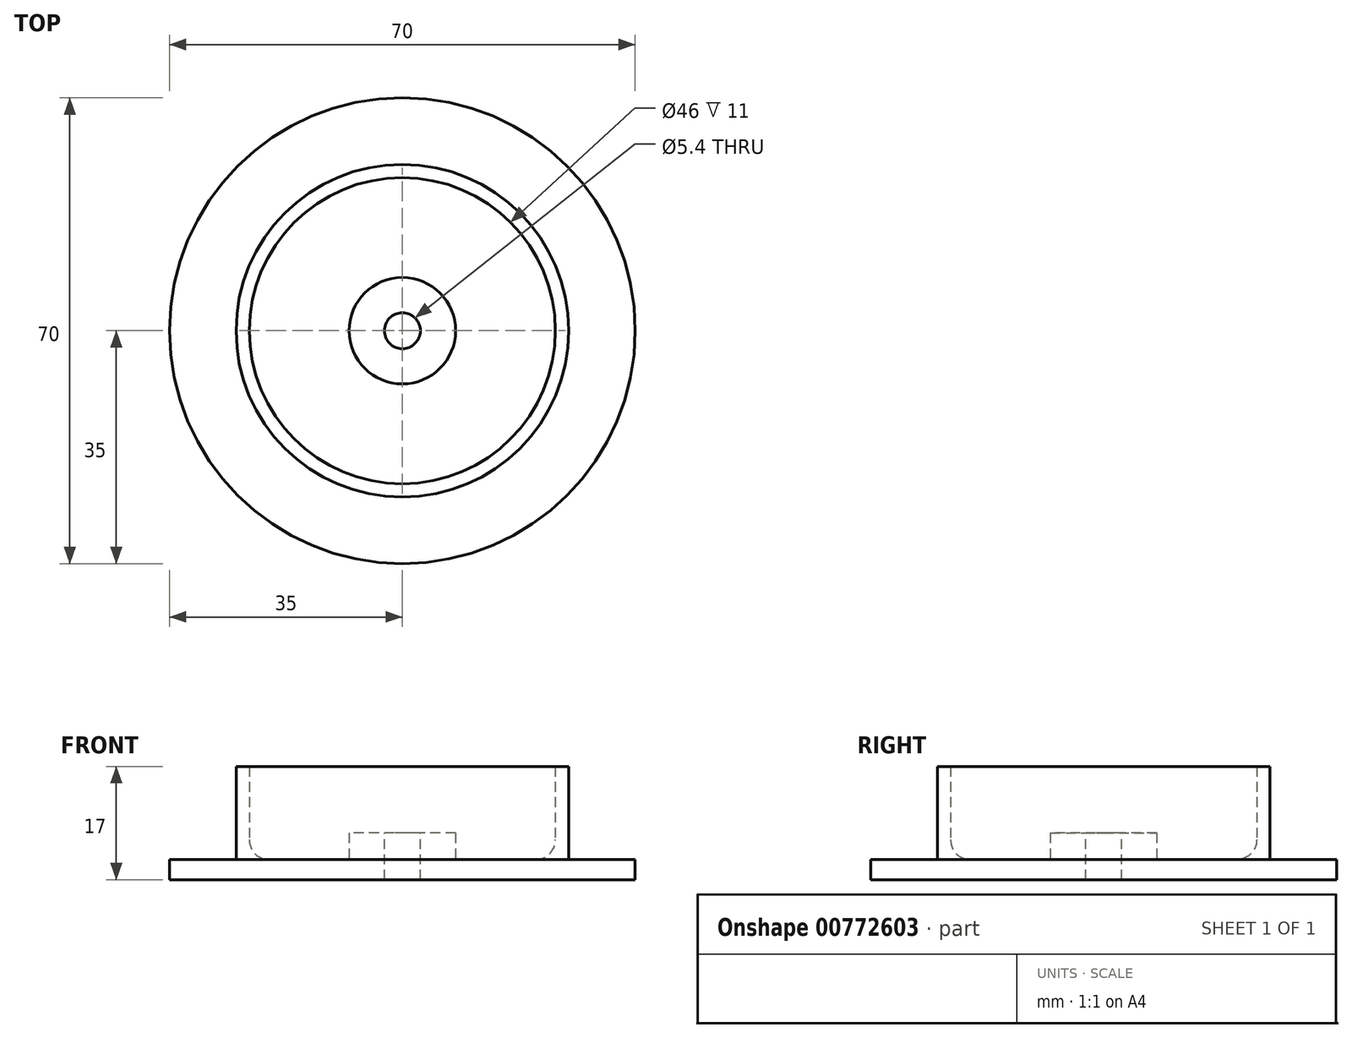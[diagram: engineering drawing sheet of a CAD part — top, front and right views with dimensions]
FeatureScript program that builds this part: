
annotation { "Feature Type Name" : "Feature", "Feature Type Description" : "" }
export const myFeature = defineFeature(function(context is Context, id is Id, definition is map)
    precondition{}
    {
        {
            var Q0;
            Q0=qCreatedBy(makeId("Top.planeOp"),FACE);
            var sketch = newSketch(context, id + "F0", { "sketchPlane" : qUnion([Q0])});
            skCircle(sketch, "E0", {"center": v(0, 0) * mm, "radius": 35 * mm});
            skSolve(sketch);
        }
        {
            var Q0;
            Q0 = qSketchRegion(id + "F0", true);
            extrude(context, id + "F1", {"entities" : qUnion([Q0]), "depth" : 3 * mm, "offsetDistance" : 25 * mm});
        }
        {
            var Q0;
            Q0=makeQuery(id+"F1.opExtrude","CAP_FACE",FACE,{"disambiguationData":[OSD([sQuery(id+"F0.wireOp",EDGE,"E0")])],"isStart":false});
            var sketch = newSketch(context, id + "F2", { "sketchPlane" : qUnion([Q0])});
            skCircle(sketch, "E1", {"center": v(0, 0) * mm, "radius": 23 * mm});
            skCircle(sketch, "E2.0", {"center": v(0, 0) * mm, "radius": 25 * mm});
            skSolve(sketch);
        }
        {
            var Q0;
            Q0=makeQuery(id+"F2.imprint","IMPRINT",FACE,{"disambiguationData":[TD([[makeQuery(id+"F2.imprint","IMPRINT",EDGE,{"derivedFrom":sQuery(id+"F2.wireOp",EDGE,"E1")}),-1.0]])]});
            extrude(context, id + "F3", {"entities" : qUnion([Q0]), "operationType" : NewBodyOperationType.ADD, "depth" : 14 * mm, "offsetDistance" : 25 * mm});
        }
        {
            var Q0;
            Q0=makeQuery(id+"F3.boolean.opBoolean","SPLIT",FACE,{"disambiguationData":[TD([makeQuery(id+"F3.opExtrude","SWEPT_FACE",FACE,{"disambiguationData":[OSD([sQuery(id+"F2.wireOp",EDGE,"E1")])]})])],"derivedFrom":makeQuery(id+"F1.opExtrude","CAP_FACE",FACE,{"disambiguationData":[OSD([sQuery(id+"F0.wireOp",EDGE,"E0")])],"isStart":false})});
            var sketch = newSketch(context, id + "F4", { "sketchPlane" : qUnion([Q0])});
            skCircle(sketch, "E3", {"center": v(0, 0) * mm, "radius": 8 * mm});
            skSolve(sketch);
        }
        {
            var Q0;
            Q0=makeQuery(id+"F4.imprint","IMPRINT",FACE,{"disambiguationData":[TD([[makeQuery(id+"F4.imprint","IMPRINT",EDGE,{"derivedFrom":sQuery(id+"F4.wireOp",EDGE,"E3")}),1.0]])]});
            extrude(context, id + "F5", {"entities" : qUnion([Q0]), "operationType" : NewBodyOperationType.ADD, "depth" : 4 * mm, "offsetDistance" : 25 * mm});
        }
        {
            var Q0;
            Q0=makeQuery(id+"F5.opExtrude","CAP_FACE",FACE,{"disambiguationData":[OSD([sQuery(id+"F4.wireOp",EDGE,"E3")])],"isStart":false});
            var sketch = newSketch(context, id + "F6", { "sketchPlane" : qUnion([Q0])});
            skCircle(sketch, "E4", {"center": v(0, 0) * mm, "radius": 2.7 * mm});
            skSolve(sketch);
        }
        {
            var Q0;
            Q0=makeQuery(id+"F6.imprint","IMPRINT",FACE,{"disambiguationData":[TD([[makeQuery(id+"F6.imprint","IMPRINT",EDGE,{"derivedFrom":sQuery(id+"F6.wireOp",EDGE,"E4")}),1.0]])]});
            extrude(context, id + "F7", {"entities" : qUnion([Q0]), "operationType" : NewBodyOperationType.REMOVE, "oppositeDirection" : true, "depth" : 25 * mm, "offsetDistance" : 25 * mm});
        }
        {
            var Q0;
            Q0=makeQuery(id+"F3.opExtrude","CAP_EDGE",EDGE,{"disambiguationData":[OSD([sQuery(id+"F2.wireOp",EDGE,"E1")])],"isStart":true});
            var Q1;
            Q1=makeQuery(id+"F5.opExtrude","CAP_EDGE",EDGE,{"disambiguationData":[OSD([sQuery(id+"F4.wireOp",EDGE,"E3")])],"isStart":true});
            fillet(context, id + "F8", {"entities" : qUnion([Q0, Q1]), "radius" : 3 * mm, "tangentPropagation" : true, "allowEdgeOverflow" : false});
        }
    });
